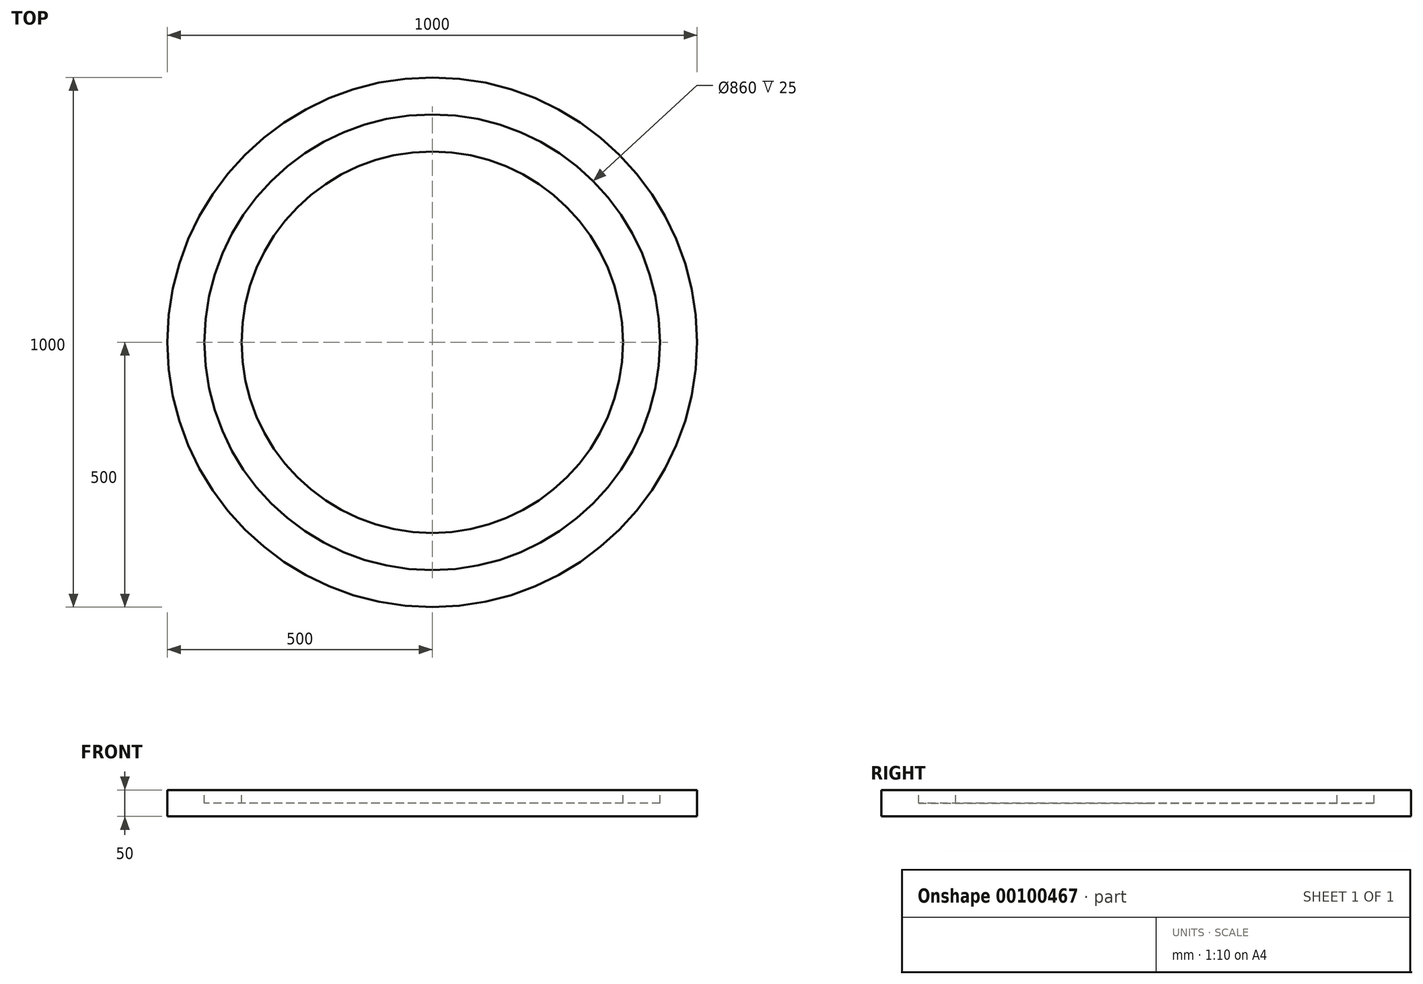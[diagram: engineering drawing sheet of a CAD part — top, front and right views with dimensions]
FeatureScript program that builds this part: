
annotation { "Feature Type Name" : "Feature", "Feature Type Description" : "" }
export const myFeature = defineFeature(function(context is Context, id is Id, definition is map)
    precondition{}
    {
        {
            var Q0;
            Q0=qCreatedBy(makeId("Top.planeOp"),FACE);
            var sketch = newSketch(context, id + "F0", { "sketchPlane" : qUnion([Q0])});
            skCircle(sketch, "E0", {"center": v(0, 0) * mm, "radius": 500 * mm});
            skSolve(sketch);
        }
        {
            var Q0;
            Q0=makeQuery(id+"F0.imprint","IMPRINT",FACE,{"disambiguationData":[TD([[makeQuery(id+"F0.imprint","IMPRINT",EDGE,{"derivedFrom":sQuery(id+"F0.wireOp",EDGE,"E0")}),1.0]])]});
            extrude(context, id + "F1", {"entities" : qUnion([Q0]), "depth" : 50 * mm});
        }
        {
            var Q0;
            Q0=makeQuery(id+"F1.opExtrude","CAP_FACE",FACE,{"disambiguationData":[OSD([sQuery(id+"F0.wireOp",EDGE,"E0")])],"isStart":false});
            var sketch = newSketch(context, id + "F2", { "sketchPlane" : qUnion([Q0])});
            skCircle(sketch, "E1", {"center": v(0, 0) * mm, "radius": 430 * mm});
            skCircle(sketch, "E2", {"center": v(0, 0) * mm, "radius": 360 * mm});
            skSolve(sketch);
        }
        {
            var Q0;
            Q0=makeQuery(id+"F2.imprint","IMPRINT",FACE,{"disambiguationData":[TD([[makeQuery(id+"F2.imprint","IMPRINT",EDGE,{"derivedFrom":sQuery(id+"F2.wireOp",EDGE,"E1")}),1.0]])]});
            extrude(context, id + "F3", {"entities" : qUnion([Q0]), "operationType" : NewBodyOperationType.REMOVE, "oppositeDirection" : true, "depth" : 25 * mm});
        }
    });
